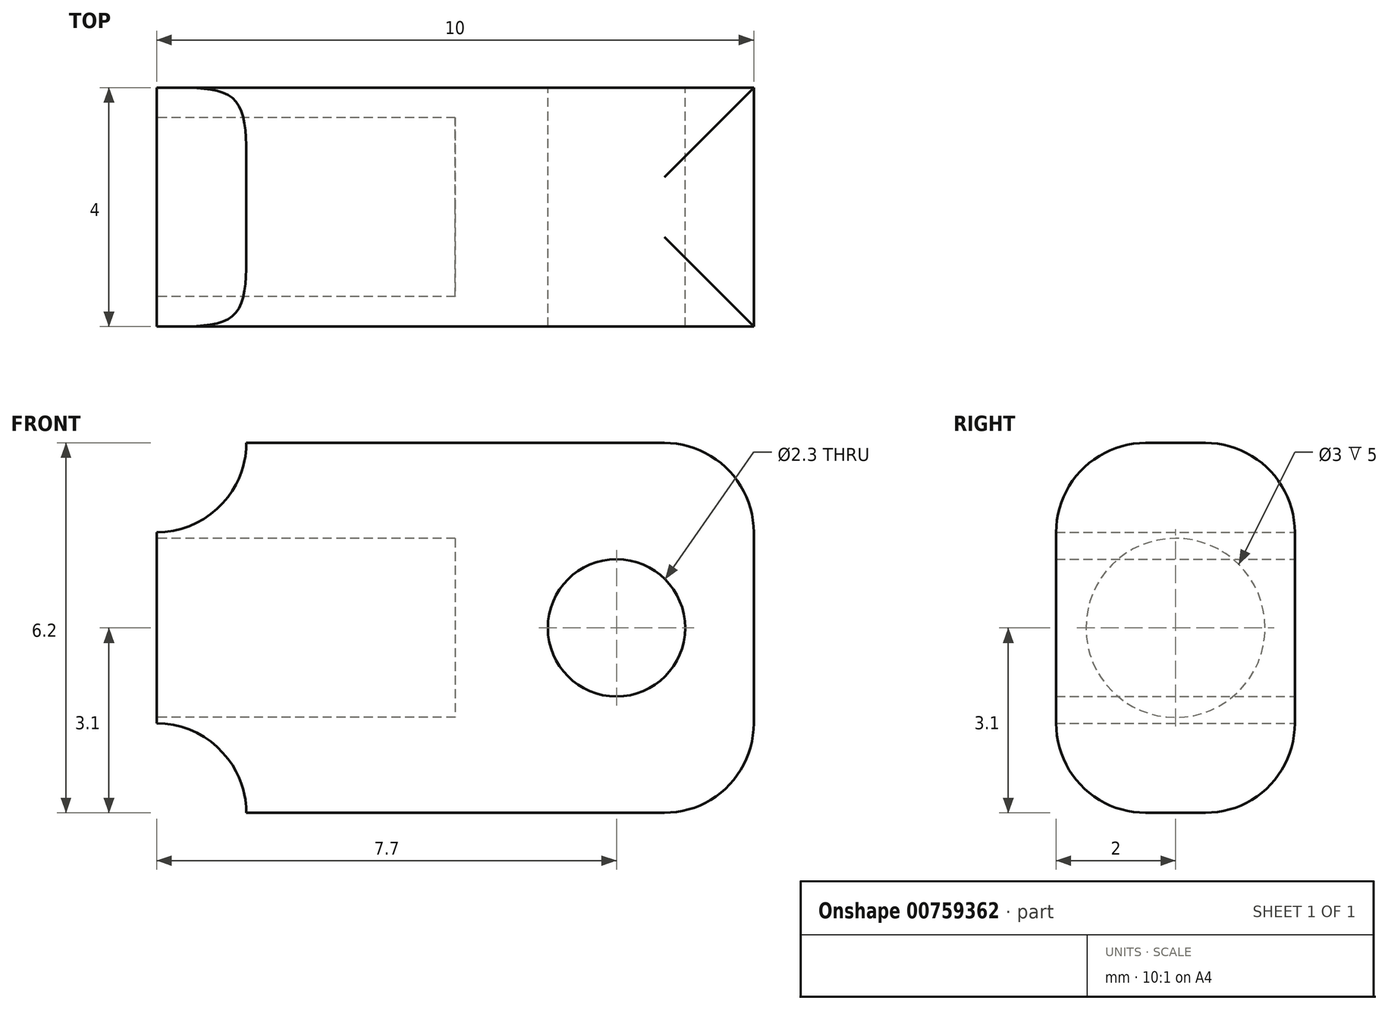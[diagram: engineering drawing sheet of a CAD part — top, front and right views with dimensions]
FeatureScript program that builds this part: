
annotation { "Feature Type Name" : "Feature", "Feature Type Description" : "" }
export const myFeature = defineFeature(function(context is Context, id is Id, definition is map)
    precondition{}
    {
        {
            var Q0;
            Q0=qCreatedBy(makeId("Front.planeOp"),FACE);
            var sketch = newSketch(context, id + "F0", { "sketchPlane" : qUnion([Q0])});
            skLineSegment(sketch, "E0.bottom", {"start": v(5, 3.1) * mm, "end": v(-3.5, 3.1) * mm});
            skLineSegment(sketch, "E0.top", {"start": v(5, -3.1) * mm, "end": v(-3.5, -3.1) * mm});
            skLineSegment(sketch, "E0.left", {"start": v(5, 3.1) * mm, "end": v(5, -3.1) * mm});
            skLineSegment(sketch, "E0.right", {"start": v(-5, 1.6) * mm, "end": v(-5, -1.6) * mm});
            skPoint(sketch, "E0.middle", {"position": v(0, 0) * mm});
            skArc(sketch, "E1", {"start": v(-5, 1.6) * mm, "mid": v(-3.94, 2.04) * mm, "end": v(-3.5, 3.1) * mm});
            skArc(sketch, "E2.MirrorCS", {"start": v(-5, -1.6) * mm, "mid": v(-3.94, -2.04) * mm, "end": v(-3.5, -3.1) * mm});
            skCircle(sketch, "E3", {"center": v(2.7, 0) * mm, "radius": 1.15 * mm});
            skSolve(sketch);
        }
        {
            var Q0;
            Q0 = qSketchRegion(id + "F0", true);
            extrude(context, id + "F1", {"entities" : qUnion([Q0]), "depth" : 4 * mm, "offsetDistance" : 25 * mm});
        }
        {
            var Q0;
            Q0=makeQuery(id+"F1.opExtrude","SWEPT_FACE",FACE,{"disambiguationData":[OSD([sQuery(id+"F0.wireOp",EDGE,"E0.right")])]});
            var sketch = newSketch(context, id + "F2", { "sketchPlane" : qUnion([Q0])});
            skCircle(sketch, "E4", {"center": v(2, 0) * mm, "radius": 1.5 * mm});
            skPoint(sketch, "E4.centerSnap0", {"position": v(2, -1.6) * mm});
            skSolve(sketch);
        }
        {
            var Q0;
            Q0 = qSketchRegion(id + "F2", true);
            extrude(context, id + "F3", {"entities" : qUnion([Q0]), "operationType" : NewBodyOperationType.REMOVE, "oppositeDirection" : true, "depth" : 5 * mm, "offsetDistance" : 25 * mm});
        }
        {
            var Q0;
            Q0=makeQuery(id+"F1.opExtrude","CAP_EDGE",EDGE,{"disambiguationData":[OSD([sQuery(id+"F0.wireOp",EDGE,"E0.bottom")])],"isStart":true});
            var Q1;
            Q1=makeQuery(id+"F1.opExtrude","SWEPT_EDGE",EDGE,{"disambiguationData":[OSD([sQuery(id+"F0.wireOp",EDGE,"E0.bottom"),sQuery(id+"F0.wireOp",EDGE,"E0.left")])]});
            var Q2;
            Q2=makeQuery(id+"F1.opExtrude","CAP_EDGE",EDGE,{"disambiguationData":[OSD([sQuery(id+"F0.wireOp",EDGE,"E0.bottom")])],"isStart":false});
            var Q3;
            Q3=makeQuery(id+"F1.opExtrude","CAP_EDGE",EDGE,{"disambiguationData":[OSD([sQuery(id+"F0.wireOp",EDGE,"E0.top")])],"isStart":false});
            var Q4;
            Q4=makeQuery(id+"F1.opExtrude","CAP_EDGE",EDGE,{"disambiguationData":[OSD([sQuery(id+"F0.wireOp",EDGE,"E0.top")])],"isStart":true});
            var Q5;
            Q5=makeQuery(id+"F1.opExtrude","SWEPT_EDGE",EDGE,{"disambiguationData":[OSD([sQuery(id+"F0.wireOp",EDGE,"E0.top"),sQuery(id+"F0.wireOp",EDGE,"E0.left")])]});
            fillet(context, id + "F4", {"entities" : qUnion([Q0, Q1, Q2, Q3, Q4, Q5]), "radius" : 1.5 * mm, "tangentPropagation" : true, "allowEdgeOverflow" : false});
        }
    });
